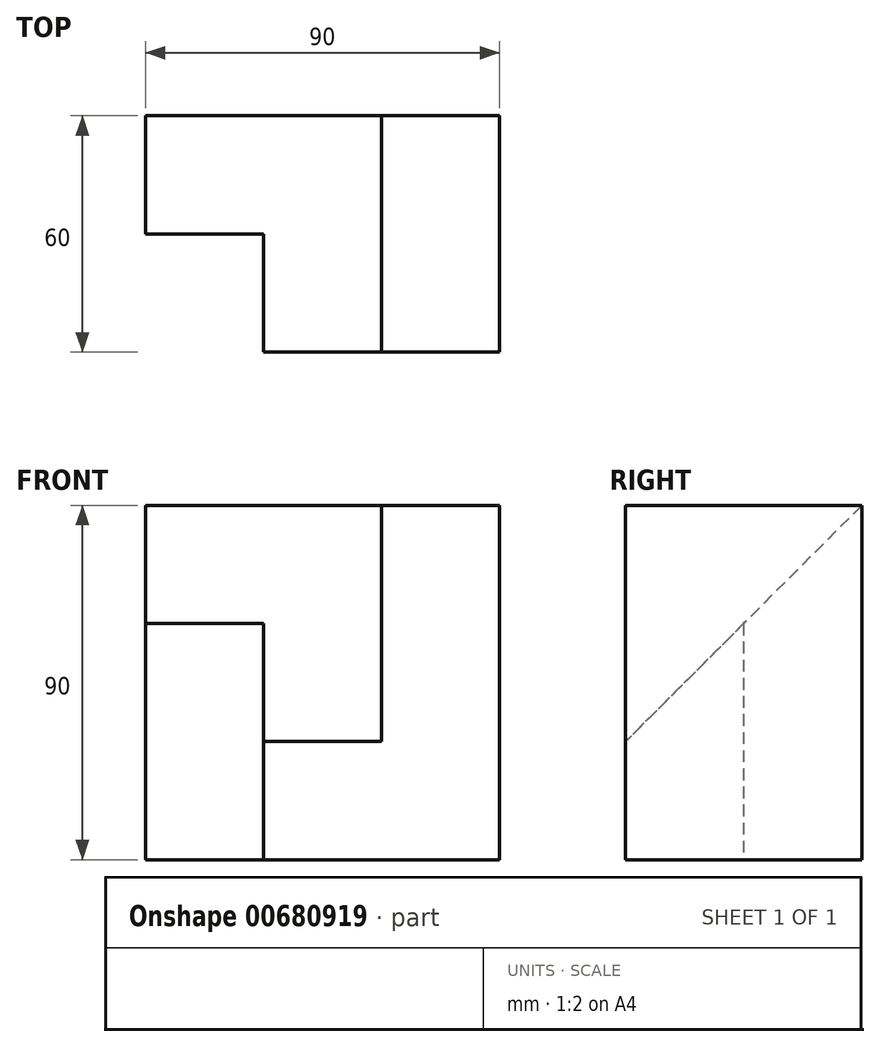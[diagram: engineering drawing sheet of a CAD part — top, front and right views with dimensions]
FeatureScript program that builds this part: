
annotation { "Feature Type Name" : "Feature", "Feature Type Description" : "" }
export const myFeature = defineFeature(function(context is Context, id is Id, definition is map)
    precondition{}
    {
        {
            var Q0;
            Q0=qCreatedBy(makeId("Front.planeOp"),FACE);
            var sketch = newSketch(context, id + "F0", { "sketchPlane" : qUnion([Q0])});
            skLineSegment(sketch, "E0.bottom", {"start": v(-71.8, 48.76) * mm, "end": v(18.2, 48.76) * mm});
            skLineSegment(sketch, "E0.top", {"start": v(-71.8, -41.24) * mm, "end": v(18.2, -41.24) * mm});
            skLineSegment(sketch, "E0.left", {"start": v(-71.8, 48.76) * mm, "end": v(-71.8, -41.24) * mm});
            skLineSegment(sketch, "E0.right", {"start": v(18.2, 48.76) * mm, "end": v(18.2, -41.24) * mm});
            skLineSegment(sketch, "E1", {"start": v(-71.8, 18.76) * mm, "end": v(-41.8, 18.76) * mm});
            skLineSegment(sketch, "E2", {"start": v(-41.8, 18.76) * mm, "end": v(-41.8, -11.24) * mm});
            skLineSegment(sketch, "E3", {"start": v(-41.8, -11.24) * mm, "end": v(-11.8, -11.24) * mm});
            skLineSegment(sketch, "E4", {"start": v(-11.8, -11.24) * mm, "end": v(-11.8, 48.76) * mm});
            skLineSegment(sketch, "E5", {"start": v(-41.8, -11.24) * mm, "end": v(-41.8, -41.24) * mm});
            skSolve(sketch);
        }
        {
            var Q0;
            {var subQ3=sQuery(id+"F0.wireOp",EDGE,"E1");Q0=makeQuery(id+"F0.imprint","IMPRINT",FACE,{"disambiguationData":[TD([[makeQuery(id+"F0.imprint","IMPRINT",EDGE,{"derivedFrom":subQ3}),-1.0]])]});}
            extrude(context, id + "F1", {"entities" : qUnion([Q0]), "depth" : 30 * mm, "offsetDistance" : 25 * mm});
        }
        {
            var Q0;
            {var subQ0=sQuery(id+"F0.wireOp",EDGE,"E0.right");Q0=makeQuery(id+"F0.imprint","IMPRINT",FACE,{"disambiguationData":[TD([[makeQuery(id+"F0.imprint","IMPRINT",EDGE,{"derivedFrom":subQ0}),-1.0]])]});}
            extrude(context, id + "F2", {"entities" : qUnion([Q0]), "operationType" : NewBodyOperationType.ADD, "depth" : 60 * mm, "offsetDistance" : 25 * mm});
        }
        {
            var Q0;
            Q0=makeQuery(id+"F2.opExtrude","SWEPT_FACE",FACE,{"disambiguationData":[OSD([sQuery(id+"F0.wireOp",EDGE,"E4")])]});
            var sketch = newSketch(context, id + "F3", { "sketchPlane" : qUnion([Q0])});
            skLineSegment(sketch, "E6", {"start": v(0, 48.76) * mm, "end": v(60, -11.24) * mm});
            skLineSegment(sketch, "E7", {"start": v(60, -11.24) * mm, "end": v(0, -11.24) * mm});
            skLineSegment(sketch, "E8", {"start": v(0, -11.24) * mm, "end": v(0, 48.76) * mm});
            skSolve(sketch);
        }
        {
            var Q0;
            Q0=makeQuery(id+"F3.imprint","IMPRINT",FACE,{"disambiguationData":[TD([[makeQuery(id+"F3.imprint","IMPRINT",EDGE,{"derivedFrom":sQuery(id+"F3.wireOp",EDGE,"E6")}),-1.0]])]});
            extrude(context, id + "F4", {"entities" : qUnion([Q0]), "operationType" : NewBodyOperationType.ADD, "depth" : 30 * mm, "offsetDistance" : 25 * mm});
        }
        {
            var Q0;
            Q0=makeQuery(id+"F4.boolean.opBoolean","SPLIT",FACE,{"derivedFrom":makeQuery(id+"F4.opExtrude","CAP_FACE",FACE,{"disambiguationData":[OSD([sQuery(id+"F3.wireOp",EDGE,"E6"),sQuery(id+"F3.wireOp",EDGE,"E7"),sQuery(id+"F3.wireOp",EDGE,"E8")])],"isStart":false})});
            extrude(context, id + "F5", {"entities" : qUnion([Q0]), "operationType" : NewBodyOperationType.ADD, "depth" : 30 * mm, "offsetDistance" : 25 * mm});
        }
    });
